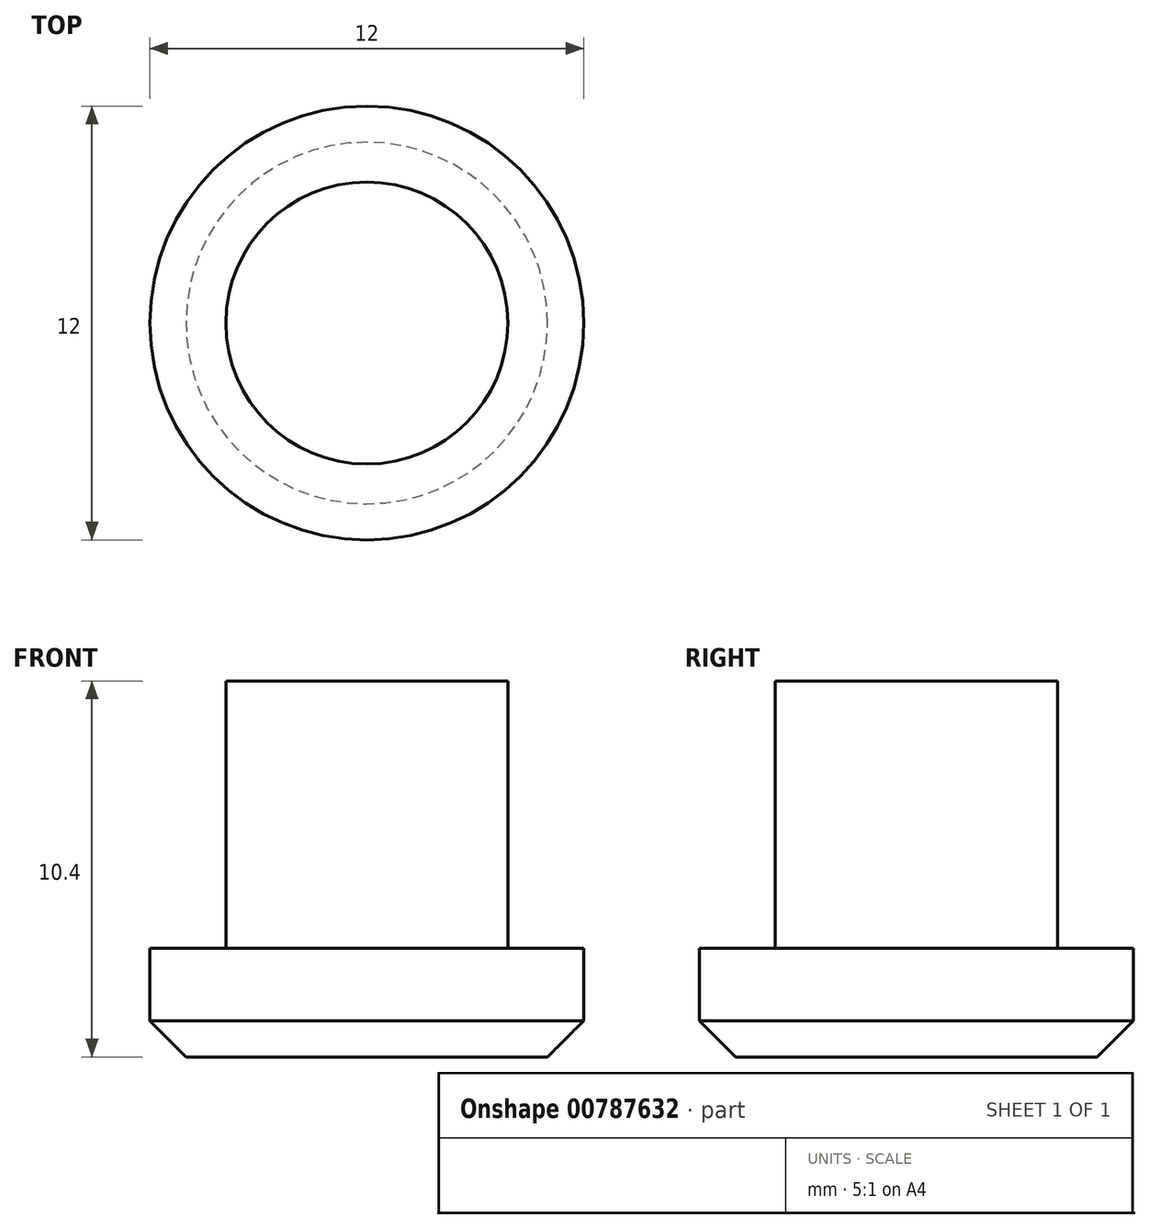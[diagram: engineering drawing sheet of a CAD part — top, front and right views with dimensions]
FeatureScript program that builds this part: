
annotation { "Feature Type Name" : "Feature", "Feature Type Description" : "" }
export const myFeature = defineFeature(function(context is Context, id is Id, definition is map)
    precondition{}
    {
        {
            var Q0;
            Q0=qCreatedBy(makeId("Top.planeOp"),FACE);
            var sketch = newSketch(context, id + "F0", { "sketchPlane" : qUnion([Q0])});
            skCircle(sketch, "E0", {"center": v(0, 0) * mm, "radius": 6 * mm});
            skSolve(sketch);
        }
        {
            var Q0;
            Q0 = qSketchRegion(id + "F0", true);
            extrude(context, id + "F1", {"entities" : qUnion([Q0]), "depth" : 3 * mm, "offsetDistance" : 25 * mm});
        }
        {
            var Q0;
            Q0=makeQuery(id+"F1.opExtrude","CAP_FACE",FACE,{"disambiguationData":[OSD([sQuery(id+"F0.wireOp",EDGE,"E0")])],"isStart":false});
            var sketch = newSketch(context, id + "F2", { "sketchPlane" : qUnion([Q0])});
            skCircle(sketch, "E1", {"center": v(0, 0) * mm, "radius": 3.9 * mm});
            skSolve(sketch);
        }
        {
            var Q0;
            Q0 = qSketchRegion(id + "F2", true);
            extrude(context, id + "F3", {"entities" : qUnion([Q0]), "operationType" : NewBodyOperationType.ADD, "depth" : 7.4 * mm, "offsetDistance" : 25 * mm});
        }
        {
            var Q0;
            Q0=makeQuery(id+"F1.opExtrude","CAP_EDGE",EDGE,{"disambiguationData":[OSD([sQuery(id+"F0.wireOp",EDGE,"E0")])],"isStart":true});
            chamfer(context, id + "F4", {"entities" : qUnion([Q0]), "width" : 1 * mm, "tangentPropagation" : true});
        }
    });
